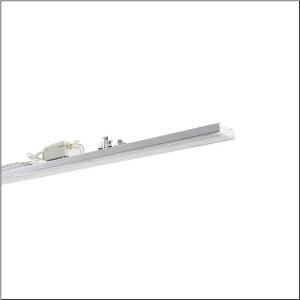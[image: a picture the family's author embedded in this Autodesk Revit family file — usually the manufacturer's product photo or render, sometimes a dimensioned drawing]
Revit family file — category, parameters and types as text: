
# Revit family: licross_r__21_recessed_mo_52tl18vn465g_e7ea
name_source: partatom
category: Lighting Fixtures
units: mm (PartAtom-declared; Revit-internal decimal feet)

## family parameters
Cut with Voids When Loaded = No
Host = Face
Light Source = No
Part Type = Normal
Room Calculation Point = No
Round Connector Dimension = Use Diameter
Shared = No

## types (1)
- --- (1 x LED, 6500 lm, 36.8 W, 4000K)
    Apparent Load = 37 VA
    CIE Flux Codes = 79 95 99 100 100
    Color Rendering = 80
    Color Temperature = 4000K
    Default Elevation = 1800 mm
    Description = Licross® 21 Recessed MO, luminaire insert, of sheet steel, galvanised, coil coated, white, length: 1.500mm, width: 66mm, height: 67mm, LED rated luminous flux: 6.500lm, light colour: 840, control gear: DALI 2, CLO, with plug, 5-pole, with phase selection, mains connection: 220..240V, AC, 50/60Hz, start of lifetime: 37W, end of service life: 44W, halogen-free wiring, primary optical cover: cover, of PMMA, light emission: direct distribution, primary light characteristic: symmetric, protection rating (complete): IP40, insulation class (complete): insulation class I (protective earthing), certification: CE, ENEC, VDE, UKCA, protection symbol: D if used in an environment without relevant dust loads with corresponding accessories, impact resistance: IK06, permissible ambient temperature for indoor applications: -25..+40°C, corresponds to IFS (International Featured Standards) requirements for safety and quality in the food industry, reducing of maximum allowable ambient temperature of 5°C with ceiling mounting, LABS conformity tested according to VDMA 24364:2018-05, packaging unit: 1 piece
    Height = 58 mm
    Lamp = 1 x LED
    Lamp Light Flux = 6500 lm
    Lamp Power = 36.8 W
    Lamp count = 1
    Length = 1500 mm
    Luminous efficacy = 177 lm/W
    Manufacturer = Siteco
    ModVariant = No
    Model = 52TL18VN465G
    Mounting Place = Ceiling
    Mounting Type = Pendant
    Number of Poles = 1
    OnlyDefault = Yes
    Power Factor = 1
    Product Name = Licross® 21 Recessed MO
    Product group = luminaire insert
    ProductGroupID = 901
    Protection Class = Protection class I
    Protection Degree = IP 40
    RLX_Detail_Level = 1
    RLX_Emergency_Light_Flux = 0 lm
    RLX_Emergency_Type = 0
    RLX_Emergency_Type_DB = No
    RlxData = <blob elided: 24653 chars, md5=1cb2cb4c>
    Socket = socket
    Standby Power = 0 W
    System Light Flux = 6500 lm
    System Power = 37 W
    Type Comments = factory setting: luminous flux: 100 % | dim-lin: 254 | 246 mA
    Type Image = l_1296930.jpg
    URL = http://relux.com
    VarID = @adj_051431
    Voltage = 0 V
    Weight = 0.00 kg
    Width = 66 mm

## geometry (parser evidence)
native form markers: Blend x4, Sweep x12
no freeform markers — native parametric forms only
